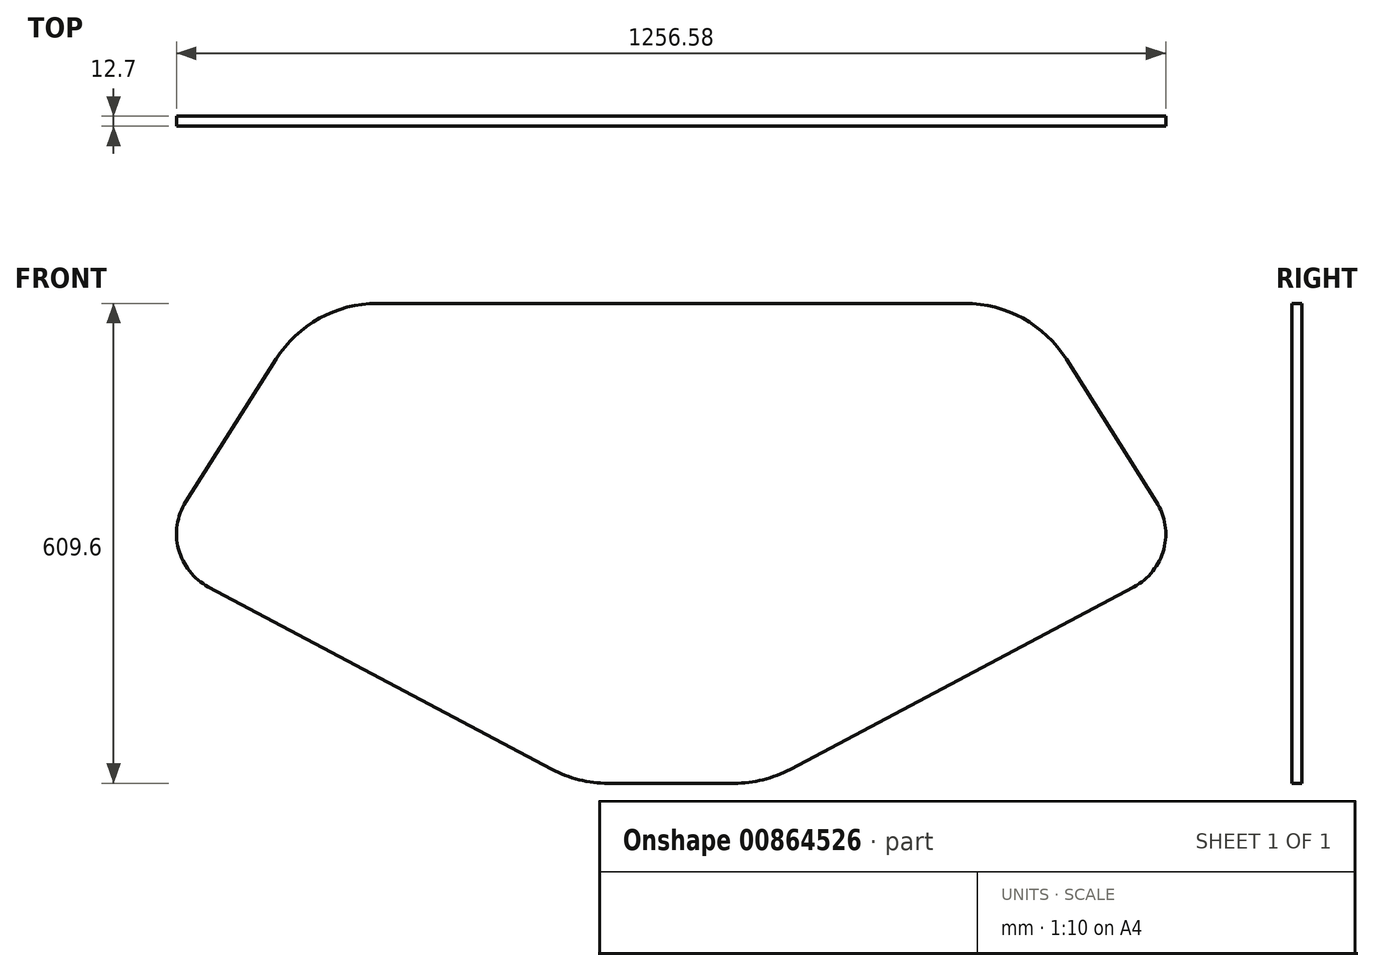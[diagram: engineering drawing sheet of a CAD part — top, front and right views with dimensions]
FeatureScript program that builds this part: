
annotation { "Feature Type Name" : "Feature", "Feature Type Description" : "" }
export const myFeature = defineFeature(function(context is Context, id is Id, definition is map)
    precondition{}
    {
        {
            var Q0;
            Q0=qCreatedBy(makeId("Front.planeOp"),FACE);
            var sketch = newSketch(context, id + "F0", { "sketchPlane" : qUnion([Q0])});
            skLineSegment(sketch, "E0", {"start": v(0, 321.54) * mm, "end": v(373.23, 321.54) * mm});
            skLineSegment(sketch, "E1", {"start": v(502.06, 250.56) * mm, "end": v(616.5, 69.46) * mm});
            skLineSegment(sketch, "E2", {"start": v(587.83, -38.54) * mm, "end": v(151.6, -270.25) * mm});
            skLineSegment(sketch, "E3.MirrorCS", {"start": v(0, 321.54) * mm, "end": v(-373.23, 321.54) * mm});
            skLineSegment(sketch, "E4.MirrorCS", {"start": v(-502.06, 250.56) * mm, "end": v(-616.5, 69.46) * mm});
            skLineSegment(sketch, "E5.MirrorCS", {"start": v(-587.83, -38.54) * mm, "end": v(-151.6, -270.25) * mm});
            skLineSegment(sketch, "E6", {"start": v(-80.1, -288.06) * mm, "end": v(80.1, -288.06) * mm});
            skPoint(sketch, "E7.orphan", {"position": v(0, -350.77) * mm});
            skPoint(sketch, "E8.visualSharp", {"position": v(-660.4, 0) * mm});
            skArc(sketch, "E8.filletArc", {"start": v(-616.5, 69.46) * mm, "mid": v(-625.74, 9.2) * mm, "end": v(-587.83, -38.54) * mm});
            skPoint(sketch, "E9.visualSharp", {"position": v(660.4, 0) * mm});
            skArc(sketch, "E9.filletArc", {"start": v(587.83, -38.54) * mm, "mid": v(625.74, 9.2) * mm, "end": v(616.5, 69.46) * mm});
            skPoint(sketch, "E10.visualSharp", {"position": v(-457.2, 321.54) * mm});
            skArc(sketch, "E10.filletArc", {"start": v(-373.23, 321.54) * mm, "mid": v(-446.77, 302.62) * mm, "end": v(-502.06, 250.56) * mm});
            skPoint(sketch, "E11.visualSharp", {"position": v(457.2, 321.54) * mm});
            skArc(sketch, "E11.filletArc", {"start": v(502.06, 250.56) * mm, "mid": v(446.77, 302.62) * mm, "end": v(373.23, 321.54) * mm});
            skPoint(sketch, "E12.visualSharp", {"position": v(118.07, -288.06) * mm});
            skArc(sketch, "E12.filletArc", {"start": v(80.1, -288.06) * mm, "mid": v(116.95, -283.54) * mm, "end": v(151.6, -270.25) * mm});
            skPoint(sketch, "E13.visualSharp", {"position": v(-118.07, -288.06) * mm});
            skArc(sketch, "E13.filletArc", {"start": v(-151.6, -270.25) * mm, "mid": v(-116.95, -283.54) * mm, "end": v(-80.1, -288.06) * mm});
            skSolve(sketch);
        }
        {
            var Q0;
            Q0=makeQuery(id+"F0.imprint","IMPRINT",FACE,{"disambiguationData":[TD([[makeQuery(id+"F0.imprint","IMPRINT",EDGE,{"derivedFrom":sQuery(id+"F0.wireOp",EDGE,"E0")}),-1.0]])]});
            extrude(context, id + "F1", {"entities" : qUnion([Q0]), "depth" : 12.7 * mm, "offsetDistance" : 25.4 * mm});
        }
    });
